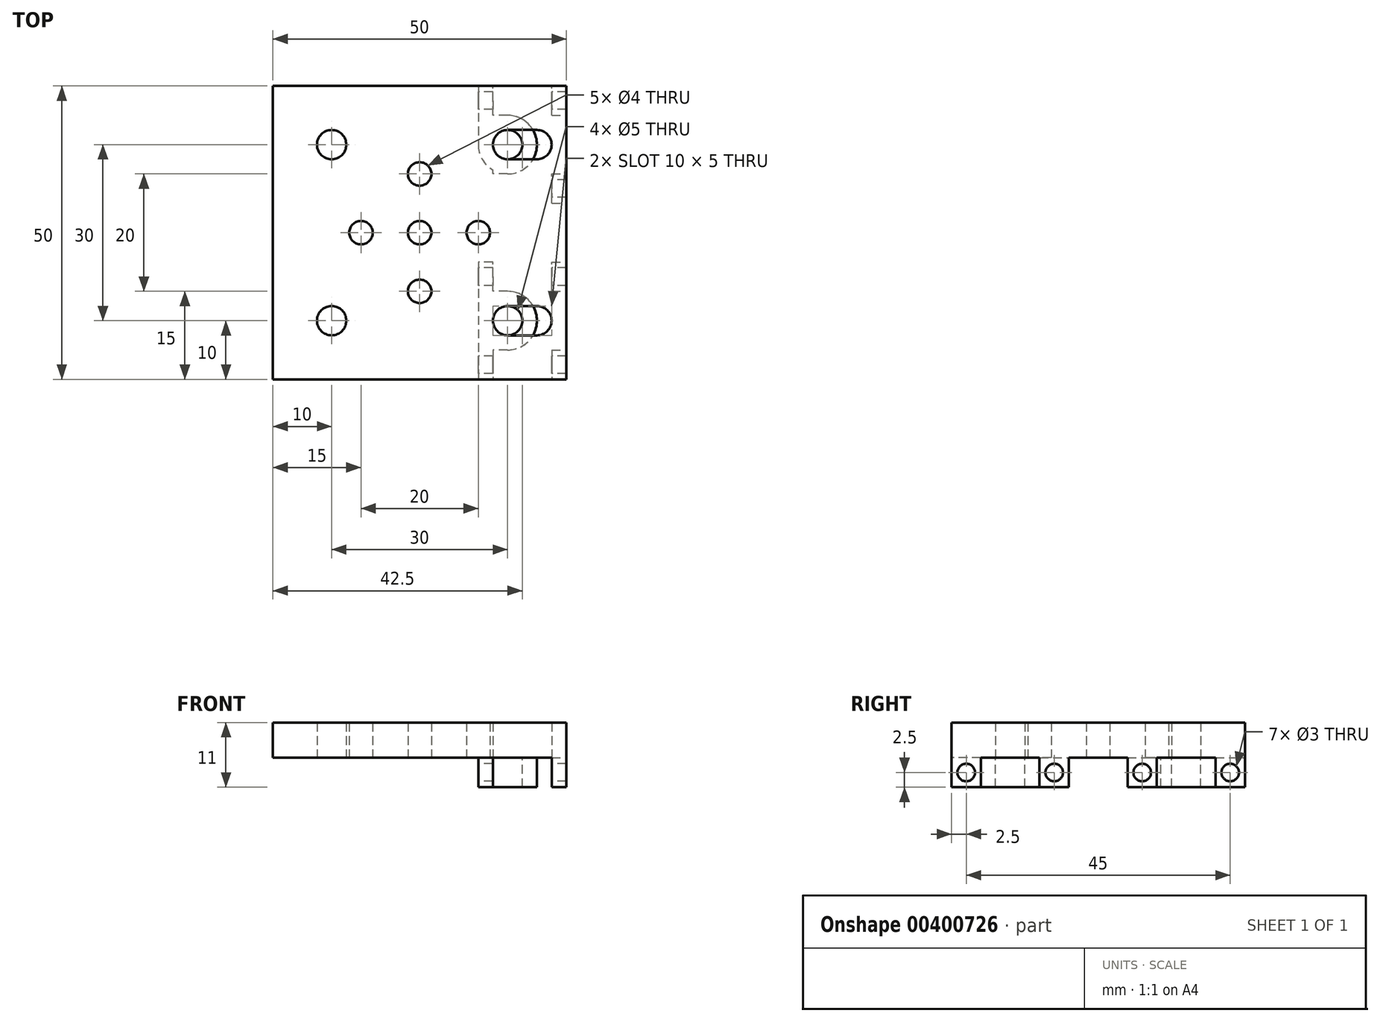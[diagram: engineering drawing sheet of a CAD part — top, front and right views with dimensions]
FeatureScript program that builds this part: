
annotation { "Feature Type Name" : "Feature", "Feature Type Description" : "" }
export const myFeature = defineFeature(function(context is Context, id is Id, definition is map)
    precondition{}
    {
        {
            var Q0;
            Q0=qCreatedBy(makeId("Top.planeOp"),FACE);
            var sketch = newSketch(context, id + "F0", { "sketchPlane" : qUnion([Q0])});
            skLineSegment(sketch, "E0.bottom", {"start": v(25, 25) * mm, "end": v(-25, 25) * mm});
            skLineSegment(sketch, "E0.top", {"start": v(25, -25) * mm, "end": v(-25, -25) * mm});
            skLineSegment(sketch, "E0.left", {"start": v(25, 25) * mm, "end": v(25, -25) * mm});
            skLineSegment(sketch, "E0.right", {"start": v(-25, 25) * mm, "end": v(-25, -25) * mm});
            skPoint(sketch, "E0.middle", {"position": v(0, 0) * mm});
            skLineSegment(sketch, "E1", {"start": v(-15, 15) * mm, "end": v(-25, 15) * mm});
            skLineSegment(sketch, "E2", {"start": v(-25, -15) * mm, "end": v(-15, -15) * mm});
            skLineSegment(sketch, "E3", {"start": v(25, 15) * mm, "end": v(20, 15) * mm});
            skCircle(sketch, "E4", {"center": v(-15, 15) * mm, "radius": 2.5 * mm});
            skCircle(sketch, "E5", {"center": v(-15, -15) * mm, "radius": 2.5 * mm});
            skArc(sketch, "E6", {"start": v(20, 12.5) * mm, "mid": v(22.5, 15) * mm, "end": v(20, 17.5) * mm});
            skLineSegment(sketch, "E7", {"start": v(20, 15) * mm, "end": v(20, 17.5) * mm});
            skLineSegment(sketch, "E8", {"start": v(20, 17.5) * mm, "end": v(20, 15) * mm});
            skLineSegment(sketch, "E9", {"start": v(20, 12.5) * mm, "end": v(20, 15) * mm});
            skLineSegment(sketch, "E10", {"start": v(20, 17.5) * mm, "end": v(15, 17.5) * mm});
            skLineSegment(sketch, "E11", {"start": v(20, 12.5) * mm, "end": v(15, 12.5) * mm});
            skArc(sketch, "E12", {"start": v(15, 17.5) * mm, "mid": v(12.5, 15) * mm, "end": v(15, 12.5) * mm});
            skLineSegment(sketch, "E13", {"start": v(25, -15) * mm, "end": v(20, -15) * mm});
            skArc(sketch, "E14", {"start": v(20, -17.5) * mm, "mid": v(22.5, -15) * mm, "end": v(20, -12.5) * mm});
            skLineSegment(sketch, "E15", {"start": v(20, -15) * mm, "end": v(20, -12.5) * mm});
            skLineSegment(sketch, "E16", {"start": v(20, -12.5) * mm, "end": v(20, -15) * mm});
            skLineSegment(sketch, "E17", {"start": v(20, -17.5) * mm, "end": v(20, -15) * mm});
            skLineSegment(sketch, "E18", {"start": v(20, -12.5) * mm, "end": v(15, -12.5) * mm});
            skLineSegment(sketch, "E19", {"start": v(20, -17.5) * mm, "end": v(15, -17.5) * mm});
            skArc(sketch, "E20", {"start": v(15, -12.5) * mm, "mid": v(12.5, -15) * mm, "end": v(15, -17.5) * mm});
            skCircle(sketch, "E21", {"center": v(0, 0) * mm, "radius": 2 * mm});
            skCircle(sketch, "E22", {"center": v(-10, 0) * mm, "radius": 2 * mm});
            skCircle(sketch, "E23", {"center": v(0, 10) * mm, "radius": 2 * mm});
            skCircle(sketch, "E24", {"center": v(10, 0) * mm, "radius": 2 * mm});
            skCircle(sketch, "E25", {"center": v(0, -10) * mm, "radius": 2 * mm});
            skSolve(sketch);
        }
        {
            var Q0;
            {var subQ4=sQuery(id+"F0.wireOp",EDGE,"E0.bottom");Q0=makeQuery(id+"F0.imprint","IMPRINT",FACE,{"disambiguationData":[TD([[makeQuery(id+"F0.imprint","IMPRINT",EDGE,{"derivedFrom":subQ4}),1.0]])]});}
            extrude(context, id + "F1", {"entities" : qUnion([Q0]), "depth" : 6 * mm});
        }
        {
            var Q0;
            Q0=makeQuery(id+"F1.opExtrude","CAP_FACE",FACE,{"disambiguationData":[OSD([sQuery(id+"F0.wireOp",EDGE,"E0.bottom"),sQuery(id+"F0.wireOp",EDGE,"E0.top"),sQuery(id+"F0.wireOp",EDGE,"E0.left"),sQuery(id+"F0.wireOp",EDGE,"E0.right"),sQuery(id+"F0.wireOp",EDGE,"E4"),sQuery(id+"F0.wireOp",EDGE,"E5"),sQuery(id+"F0.wireOp",EDGE,"E6"),sQuery(id+"F0.wireOp",EDGE,"E10"),sQuery(id+"F0.wireOp",EDGE,"E11"),sQuery(id+"F0.wireOp",EDGE,"E12"),sQuery(id+"F0.wireOp",EDGE,"E14"),sQuery(id+"F0.wireOp",EDGE,"E18"),sQuery(id+"F0.wireOp",EDGE,"E19"),sQuery(id+"F0.wireOp",EDGE,"E20"),sQuery(id+"F0.wireOp",EDGE,"E21"),sQuery(id+"F0.wireOp",EDGE,"E22"),sQuery(id+"F0.wireOp",EDGE,"E23"),sQuery(id+"F0.wireOp",EDGE,"E24"),sQuery(id+"F0.wireOp",EDGE,"E25")])],"isStart":true});
            var sketch = newSketch(context, id + "F2", { "sketchPlane" : qUnion([Q0])});
            skLineSegment(sketch, "E26", {"start": v(22.5, 15) * mm, "end": v(22.5, 25) * mm});
            skLineSegment(sketch, "E27", {"start": v(22.5, 15) * mm, "end": v(22.5, -15) * mm});
            skLineSegment(sketch, "E28", {"start": v(22.5, -15) * mm, "end": v(22.5, -25) * mm});
            skLineSegment(sketch, "E29", {"start": v(22.5, -15) * mm, "end": v(22.5, -5) * mm});
            skLineSegment(sketch, "E30", {"start": v(22.5, 15) * mm, "end": v(22.5, 5) * mm});
            skLineSegment(sketch, "E31", {"start": v(22.5, 5) * mm, "end": v(25, 5) * mm});
            skLineSegment(sketch, "E32", {"start": v(22.5, -5) * mm, "end": v(25, -5) * mm});
            skLineSegment(sketch, "E33", {"start": v(22.5, 20) * mm, "end": v(25, 20) * mm});
            skLineSegment(sketch, "E34", {"start": v(22.5, 10) * mm, "end": v(25, 10) * mm});
            skLineSegment(sketch, "E35", {"start": v(22.5, -10) * mm, "end": v(25, -10) * mm});
            skLineSegment(sketch, "E36", {"start": v(22.5, -20) * mm, "end": v(25, -20) * mm});
            skSolve(sketch);
        }
        {
            var Q0;
            {var subQ2=sQuery(id+"F2.wireOp",EDGE,"E26");Q0=makeQuery(id+"F2.imprint","IMPRINT",FACE,{"disambiguationData":[TD([[makeQuery(id+"F2.imprint","IMPRINT",EDGE,{"derivedFrom":subQ2}),-1.0]])]});}
            var Q1;
            {var subQ3=sQuery(id+"F2.wireOp",EDGE,"E28");Q1=makeQuery(id+"F2.imprint","IMPRINT",FACE,{"disambiguationData":[TD([[makeQuery(id+"F2.imprint","IMPRINT",EDGE,{"derivedFrom":subQ3}),1.0]])]});}
            var Q2;
            {var subQ0=sQuery(id+"F2.wireOp",EDGE,"E32");Q2=makeQuery(id+"F2.imprint","IMPRINT",FACE,{"disambiguationData":[TD([[makeQuery(id+"F2.imprint","IMPRINT",EDGE,{"derivedFrom":subQ0}),-1.0]])]});}
            var Q3;
            {var subQ0=sQuery(id+"F2.wireOp",EDGE,"E31");Q3=makeQuery(id+"F2.imprint","IMPRINT",FACE,{"disambiguationData":[TD([[makeQuery(id+"F2.imprint","IMPRINT",EDGE,{"derivedFrom":subQ0}),1.0]])]});}
            extrude(context, id + "F3", {"entities" : qUnion([Q0, Q1, Q2, Q3]), "operationType" : NewBodyOperationType.ADD, "depth" : 5 * mm});
        }
        {
            var Q0;
            Q0=makeQuery(id+"F1.opExtrude","CAP_FACE",FACE,{"disambiguationData":[OSD([sQuery(id+"F0.wireOp",EDGE,"E0.bottom"),sQuery(id+"F0.wireOp",EDGE,"E0.top"),sQuery(id+"F0.wireOp",EDGE,"E0.left"),sQuery(id+"F0.wireOp",EDGE,"E0.right"),sQuery(id+"F0.wireOp",EDGE,"E4"),sQuery(id+"F0.wireOp",EDGE,"E5"),sQuery(id+"F0.wireOp",EDGE,"E6"),sQuery(id+"F0.wireOp",EDGE,"E10"),sQuery(id+"F0.wireOp",EDGE,"E11"),sQuery(id+"F0.wireOp",EDGE,"E12"),sQuery(id+"F0.wireOp",EDGE,"E14"),sQuery(id+"F0.wireOp",EDGE,"E18"),sQuery(id+"F0.wireOp",EDGE,"E19"),sQuery(id+"F0.wireOp",EDGE,"E20"),sQuery(id+"F0.wireOp",EDGE,"E21"),sQuery(id+"F0.wireOp",EDGE,"E22"),sQuery(id+"F0.wireOp",EDGE,"E23"),sQuery(id+"F0.wireOp",EDGE,"E24"),sQuery(id+"F0.wireOp",EDGE,"E25")])],"isStart":true});
            var sketch = newSketch(context, id + "F4", { "sketchPlane" : qUnion([Q0])});
            skLineSegment(sketch, "E37", {"start": v(12.5, 15) * mm, "end": v(12.5, 25) * mm});
            skLineSegment(sketch, "E38", {"start": v(12.5, 15) * mm, "end": v(12.5, -15) * mm});
            skLineSegment(sketch, "E39", {"start": v(12.5, -15) * mm, "end": v(12.5, -25) * mm});
            skLineSegment(sketch, "E40", {"start": v(10, -25) * mm, "end": v(10, 25) * mm});
            skLineSegment(sketch, "E41", {"start": v(15, -15) * mm, "end": v(12.5, -15) * mm});
            skLineSegment(sketch, "E42", {"start": v(15, 15) * mm, "end": v(12.5, 15) * mm});
            skCircle(sketch, "E43", {"center": v(15, 15) * mm, "radius": 2.5 * mm});
            skCircle(sketch, "E44", {"center": v(15, -15) * mm, "radius": 2.5 * mm});
            skCircle(sketch, "E45", {"center": v(15, -15) * mm, "radius": 5 * mm});
            skCircle(sketch, "E46", {"center": v(15, 15) * mm, "radius": 5 * mm});
            skLineSegment(sketch, "E47", {"start": v(15, -20) * mm, "end": v(12.5, -20) * mm});
            skLineSegment(sketch, "E48", {"start": v(15, -10) * mm, "end": v(12.5, -10) * mm});
            skLineSegment(sketch, "E49", {"start": v(15, 10) * mm, "end": v(12.5, 10) * mm});
            skLineSegment(sketch, "E50", {"start": v(15, 20) * mm, "end": v(12.5, 20) * mm});
            skLineSegment(sketch, "E51", {"start": v(12.5, -10) * mm, "end": v(12.5, -5) * mm});
            skLineSegment(sketch, "E52", {"start": v(12.5, -5) * mm, "end": v(22.5, -5) * mm});
            skLineSegment(sketch, "E53", {"start": v(12.5, 10) * mm, "end": v(12.5, 5) * mm});
            skLineSegment(sketch, "E54", {"start": v(12.5, 5) * mm, "end": v(22.5, 5) * mm});
            skLineSegment(sketch, "E55", {"start": v(12.5, -5) * mm, "end": v(10, -5) * mm});
            skLineSegment(sketch, "E56", {"start": v(12.5, 5) * mm, "end": v(10, 5) * mm});
            skSolve(sketch);
        }
        {
            var Q0;
            {var subQ7=sQuery(id+"F4.wireOp",EDGE,"E37");Q0=makeQuery(id+"F4.imprint","IMPRINT",FACE,{"disambiguationData":[TD([[makeQuery(id+"F4.imprint","IMPRINT",EDGE,{"derivedFrom":subQ7}),1.0]])]});}
            var Q1;
            {var subQ1=sQuery(id+"F4.wireOp",EDGE,"E37");var subQ3=sQuery(id+"F4.wireOp",EDGE,"E46");var subQ4=makeQuery(id+"F4.imprint","INTERSECT",VERTEX,{"derivedFrom":[subQ1,subQ3]});Q1=makeQuery(id+"F4.imprint","IMPRINT",FACE,{"disambiguationData":[TD([[makeQuery(id+"F4.imprint","IMPRINT",EDGE,{"disambiguationData":[TD([[subQ4,-1.0]])],"derivedFrom":subQ3}),1.0]])]});}
            var Q2;
            {var subQ0=sQuery(id+"F4.wireOp",EDGE,"E46");var subQ1=makeQuery(id+"F4.imprint","INTERSECT",VERTEX,{"derivedFrom":[subQ0,sQuery(id+"F4.wireOp",EDGE,"E49")]});Q2=makeQuery(id+"F4.imprint","IMPRINT",FACE,{"disambiguationData":[TD([[makeQuery(id+"F4.imprint","IMPRINT",EDGE,{"disambiguationData":[TD([[subQ1,1.0]])],"derivedFrom":subQ0}),1.0]])]});}
            var Q3;
            {var subQ0=sQuery(id+"F4.wireOp",EDGE,"E50");Q3=makeQuery(id+"F4.imprint","IMPRINT",FACE,{"disambiguationData":[TD([[makeQuery(id+"F4.imprint","IMPRINT",EDGE,{"derivedFrom":subQ0}),1.0]])]});}
            var Q4;
            {var subQ0=sQuery(id+"F4.wireOp",EDGE,"E46");var subQ1=makeQuery(id+"F4.imprint","INTERSECT",VERTEX,{"derivedFrom":[subQ0,sQuery(id+"F4.wireOp",EDGE,"E50")]});Q4=makeQuery(id+"F4.imprint","IMPRINT",FACE,{"disambiguationData":[TD([[makeQuery(id+"F4.imprint","IMPRINT",EDGE,{"disambiguationData":[TD([[subQ1,1.0]])],"derivedFrom":subQ0}),1.0]])]});}
            var Q5;
            {var subQ0=sQuery(id+"F4.wireOp",EDGE,"E43");var subQ1=makeQuery(id+"F1.opExtrude","CAP_EDGE",EDGE,{"disambiguationData":[OSD([sQuery(id+"F0.wireOp",EDGE,"E18")])],"isStart":true});var subQ2=makeQuery(id+"F4.imprint","INTERSECT",VERTEX,{"derivedFrom":[subQ1,subQ0]});var subQ3=makeQuery(id+"F1.opExtrude","CAP_EDGE",EDGE,{"disambiguationData":[OSD([sQuery(id+"F0.wireOp",EDGE,"E19")])],"isStart":true});var subQ4=makeQuery(id+"F4.imprint","INTERSECT",VERTEX,{"derivedFrom":[subQ3,subQ0]});Q5=makeQuery(id+"F4.imprint","IMPRINT",FACE,{"disambiguationData":[TD([[makeQuery(id+"F4.imprint","IMPRINT",EDGE,{"disambiguationData":[TD([[subQ2,-1.0],[subQ4,1.0]])],"derivedFrom":subQ0}),-1.0]])]});}
            var Q6;
            {var subQ5=sQuery(id+"F4.wireOp",EDGE,"E38");var subQ8=makeQuery(id+"F4.imprint","INTERSECT",VERTEX,{"derivedFrom":[subQ5,sQuery(id+"F4.wireOp",EDGE,"E49")]});Q6=makeQuery(id+"F4.imprint","IMPRINT",FACE,{"disambiguationData":[TD([[makeQuery(id+"F4.imprint","IMPRINT",EDGE,{"disambiguationData":[TD([[subQ8,1.0]])],"derivedFrom":subQ5}),-1.0]])]});}
            var Q7;
            {var subQ1=sQuery(id+"F4.wireOp",EDGE,"E38");var subQ3=sQuery(id+"F4.wireOp",EDGE,"E45");var subQ4=makeQuery(id+"F4.imprint","INTERSECT",VERTEX,{"derivedFrom":[subQ1,subQ3]});Q7=makeQuery(id+"F4.imprint","IMPRINT",FACE,{"disambiguationData":[TD([[makeQuery(id+"F4.imprint","IMPRINT",EDGE,{"disambiguationData":[TD([[subQ4,-1.0]])],"derivedFrom":subQ3}),1.0]])]});}
            var Q8;
            {var subQ0=sQuery(id+"F4.wireOp",EDGE,"E45");var subQ1=makeQuery(id+"F4.imprint","INTERSECT",VERTEX,{"derivedFrom":[subQ0,sQuery(id+"F4.wireOp",EDGE,"E47")]});Q8=makeQuery(id+"F4.imprint","IMPRINT",FACE,{"disambiguationData":[TD([[makeQuery(id+"F4.imprint","IMPRINT",EDGE,{"disambiguationData":[TD([[subQ1,1.0]])],"derivedFrom":subQ0}),1.0]])]});}
            var Q9;
            {var subQ0=sQuery(id+"F4.wireOp",EDGE,"E44");var subQ1=makeQuery(id+"F1.opExtrude","CAP_EDGE",EDGE,{"disambiguationData":[OSD([sQuery(id+"F0.wireOp",EDGE,"E10")])],"isStart":true});var subQ2=makeQuery(id+"F4.imprint","INTERSECT",VERTEX,{"derivedFrom":[subQ1,subQ0]});var subQ3=makeQuery(id+"F1.opExtrude","CAP_EDGE",EDGE,{"disambiguationData":[OSD([sQuery(id+"F0.wireOp",EDGE,"E11")])],"isStart":true});var subQ4=makeQuery(id+"F4.imprint","INTERSECT",VERTEX,{"derivedFrom":[subQ3,subQ0]});Q9=makeQuery(id+"F4.imprint","IMPRINT",FACE,{"disambiguationData":[TD([[makeQuery(id+"F4.imprint","IMPRINT",EDGE,{"disambiguationData":[TD([[subQ2,-1.0],[subQ4,1.0]])],"derivedFrom":subQ0}),-1.0]])]});}
            var Q10;
            {var subQ0=sQuery(id+"F4.wireOp",EDGE,"E45");var subQ1=makeQuery(id+"F4.imprint","INTERSECT",VERTEX,{"derivedFrom":[subQ0,sQuery(id+"F4.wireOp",EDGE,"E48")]});Q10=makeQuery(id+"F4.imprint","IMPRINT",FACE,{"disambiguationData":[TD([[makeQuery(id+"F4.imprint","IMPRINT",EDGE,{"disambiguationData":[TD([[subQ1,1.0]])],"derivedFrom":subQ0}),1.0]])]});}
            var Q11;
            {var subQ1=sQuery(id+"F4.wireOp",EDGE,"E39");var subQ8=makeQuery(id+"F4.imprint","INTERSECT",VERTEX,{"derivedFrom":[subQ1,sQuery(id+"F4.wireOp",EDGE,"E47")]});Q11=makeQuery(id+"F4.imprint","IMPRINT",FACE,{"disambiguationData":[TD([[makeQuery(id+"F4.imprint","IMPRINT",EDGE,{"disambiguationData":[TD([[subQ8,1.0]])],"derivedFrom":subQ1}),-1.0]])]});}
            var Q12;
            {var subQ0=sQuery(id+"F4.wireOp",EDGE,"E51");Q12=makeQuery(id+"F4.imprint","IMPRINT",FACE,{"disambiguationData":[TD([[makeQuery(id+"F4.imprint","IMPRINT",EDGE,{"derivedFrom":subQ0}),1.0]])]});}
            var Q13;
            {var subQ0=sQuery(id+"F4.wireOp",EDGE,"E47");Q13=makeQuery(id+"F4.imprint","IMPRINT",FACE,{"disambiguationData":[TD([[makeQuery(id+"F4.imprint","IMPRINT",EDGE,{"derivedFrom":subQ0}),-1.0]])]});}
            var Q14;
            {var subQ0=sQuery(id+"F4.wireOp",EDGE,"E48");Q14=makeQuery(id+"F4.imprint","IMPRINT",FACE,{"disambiguationData":[TD([[makeQuery(id+"F4.imprint","IMPRINT",EDGE,{"derivedFrom":subQ0}),1.0]])]});}
            var Q15;
            {var subQ0=sQuery(id+"F4.wireOp",EDGE,"E49");Q15=makeQuery(id+"F4.imprint","IMPRINT",FACE,{"disambiguationData":[TD([[makeQuery(id+"F4.imprint","IMPRINT",EDGE,{"derivedFrom":subQ0}),-1.0]])]});}
            extrude(context, id + "F5", {"entities" : qUnion([Q0, Q1, Q2, Q3, Q4, Q5, Q6, Q7, Q8, Q9, Q10, Q11, Q12, Q13, Q14, Q15]), "depth" : 5 * mm});
        }
        {
            var Q0;
            {var subQ0=sQuery(id+"F4.wireOp",EDGE,"E40");Q0=makeQuery(id+"F5.opExtrude","SWEPT_FACE",FACE,{"disambiguationData":[OSD([subQ0]),TDD([makeQuery(id+"F4.imprint","IMPRINT",EDGE,{"disambiguationData":[TD([[makeQuery(id+"F4.imprint","INTERSECT",VERTEX,{"derivedFrom":[subQ0,sQuery(id+"F4.wireOp",EDGE,"E56")]}),-1.0]])],"derivedFrom":subQ0}),makeQuery(id+"F4.imprint","IMPRINT",EDGE,{"disambiguationData":[TD([[makeQuery(id+"F4.imprint","INTERSECT",VERTEX,{"derivedFrom":[makeQuery(id+"F1.opExtrude","CAP_EDGE",EDGE,{"disambiguationData":[OSD([sQuery(id+"F0.wireOp",EDGE,"E0.top")])],"isStart":true}),subQ0]}),1.0]])],"derivedFrom":subQ0})])]});}
            var sketch = newSketch(context, id + "F6", { "sketchPlane" : qUnion([Q0])});
            skLineSegment(sketch, "E57", {"start": v(5, -2.5) * mm, "end": v(7.5, -2.5) * mm});
            skLineSegment(sketch, "E58", {"start": v(25, -2.5) * mm, "end": v(22.5, -2.5) * mm});
            skSolve(sketch);
        }
        {
            var Q0;
            {var subQ0=sQuery(id+"F4.wireOp",EDGE,"E40");Q0=makeQuery(id+"F5.opExtrude","SWEPT_FACE",FACE,{"disambiguationData":[OSD([subQ0]),TDD([makeQuery(id+"F4.imprint","IMPRINT",EDGE,{"disambiguationData":[TD([[makeQuery(id+"F4.imprint","INTERSECT",VERTEX,{"derivedFrom":[makeQuery(id+"F1.opExtrude","CAP_EDGE",EDGE,{"disambiguationData":[OSD([sQuery(id+"F0.wireOp",EDGE,"E0.bottom")])],"isStart":true}),subQ0]}),-1.0]])],"derivedFrom":subQ0}),makeQuery(id+"F4.imprint","IMPRINT",EDGE,{"disambiguationData":[TD([[makeQuery(id+"F4.imprint","INTERSECT",VERTEX,{"derivedFrom":[subQ0,sQuery(id+"F4.wireOp",EDGE,"E55")]}),1.0]])],"derivedFrom":subQ0})])]});}
            var sketch = newSketch(context, id + "F7", { "sketchPlane" : qUnion([Q0])});
            skLineSegment(sketch, "E59", {"start": v(-5, -2.5) * mm, "end": v(-7.5, -2.5) * mm});
            skLineSegment(sketch, "E60", {"start": v(-25, -2.5) * mm, "end": v(-22.5, -2.5) * mm});
            skSolve(sketch);
        }
        {
            var Q0;
            Q0=sQuery(id+"F7.wireOp",VERTEX,"E59.end");
            var Q1;
            Q1=sQuery(id+"F6.wireOp",VERTEX,"E57.end");
            var Q2;
            Q2=sQuery(id+"F6.wireOp",VERTEX,"E58.end");
            var Q3;
            Q3=sQuery(id+"F7.wireOp",VERTEX,"E60.end");
            var Q4;
            Q4=makeQuery(id+"F1.opExtrude","SWEPT_BODY",BODY,{"disambiguationData":[OSD([sQuery(id+"F0.wireOp",EDGE,"E0.bottom"),sQuery(id+"F0.wireOp",EDGE,"E0.top"),sQuery(id+"F0.wireOp",EDGE,"E0.left"),sQuery(id+"F0.wireOp",EDGE,"E0.right"),sQuery(id+"F0.wireOp",EDGE,"E4"),sQuery(id+"F0.wireOp",EDGE,"E5"),sQuery(id+"F0.wireOp",EDGE,"E6"),sQuery(id+"F0.wireOp",EDGE,"E10"),sQuery(id+"F0.wireOp",EDGE,"E11"),sQuery(id+"F0.wireOp",EDGE,"E12"),sQuery(id+"F0.wireOp",EDGE,"E14"),sQuery(id+"F0.wireOp",EDGE,"E18"),sQuery(id+"F0.wireOp",EDGE,"E19"),sQuery(id+"F0.wireOp",EDGE,"E20"),sQuery(id+"F0.wireOp",EDGE,"E21"),sQuery(id+"F0.wireOp",EDGE,"E22"),sQuery(id+"F0.wireOp",EDGE,"E23"),sQuery(id+"F0.wireOp",EDGE,"E24"),sQuery(id+"F0.wireOp",EDGE,"E25")])]});
            var Q5;
            Q5=makeQuery(id+"F5.opExtrude","SWEPT_BODY",BODY,{"disambiguationData":[OSD([sQuery(id+"F0.wireOp",EDGE,"E0.bottom"),sQuery(id+"F4.wireOp",EDGE,"E39"),sQuery(id+"F4.wireOp",EDGE,"E40"),sQuery(id+"F4.wireOp",EDGE,"E44"),sQuery(id+"F4.wireOp",EDGE,"E45"),sQuery(id+"F4.wireOp",EDGE,"E47"),sQuery(id+"F4.wireOp",EDGE,"E48"),sQuery(id+"F4.wireOp",EDGE,"E51"),sQuery(id+"F4.wireOp",EDGE,"E55")])]});
            var Q6;
            Q6=makeQuery(id+"F5.opExtrude","SWEPT_BODY",BODY,{"disambiguationData":[OSD([sQuery(id+"F0.wireOp",EDGE,"E0.top"),sQuery(id+"F4.wireOp",EDGE,"E37"),sQuery(id+"F4.wireOp",EDGE,"E40"),sQuery(id+"F4.wireOp",EDGE,"E43"),sQuery(id+"F4.wireOp",EDGE,"E46"),sQuery(id+"F4.wireOp",EDGE,"E49"),sQuery(id+"F4.wireOp",EDGE,"E50"),sQuery(id+"F4.wireOp",EDGE,"E53"),sQuery(id+"F4.wireOp",EDGE,"E56")])]});
            hole(context, id + "F8", {"style" : HoleStyle.SIMPLE, "endStyle" : HoleEndStyle.BLIND, "holeDiameter" : 3 * mm, "holeDepth" : 40 * mm, "isTappedThrough" : true, "tappedDepth" : 12 * mm, "tapClearance" : 3, "locations" : qUnion([Q0, Q1, Q2, Q3]), "scope" : qUnion([Q4, Q5, Q6])});
        }
    });
